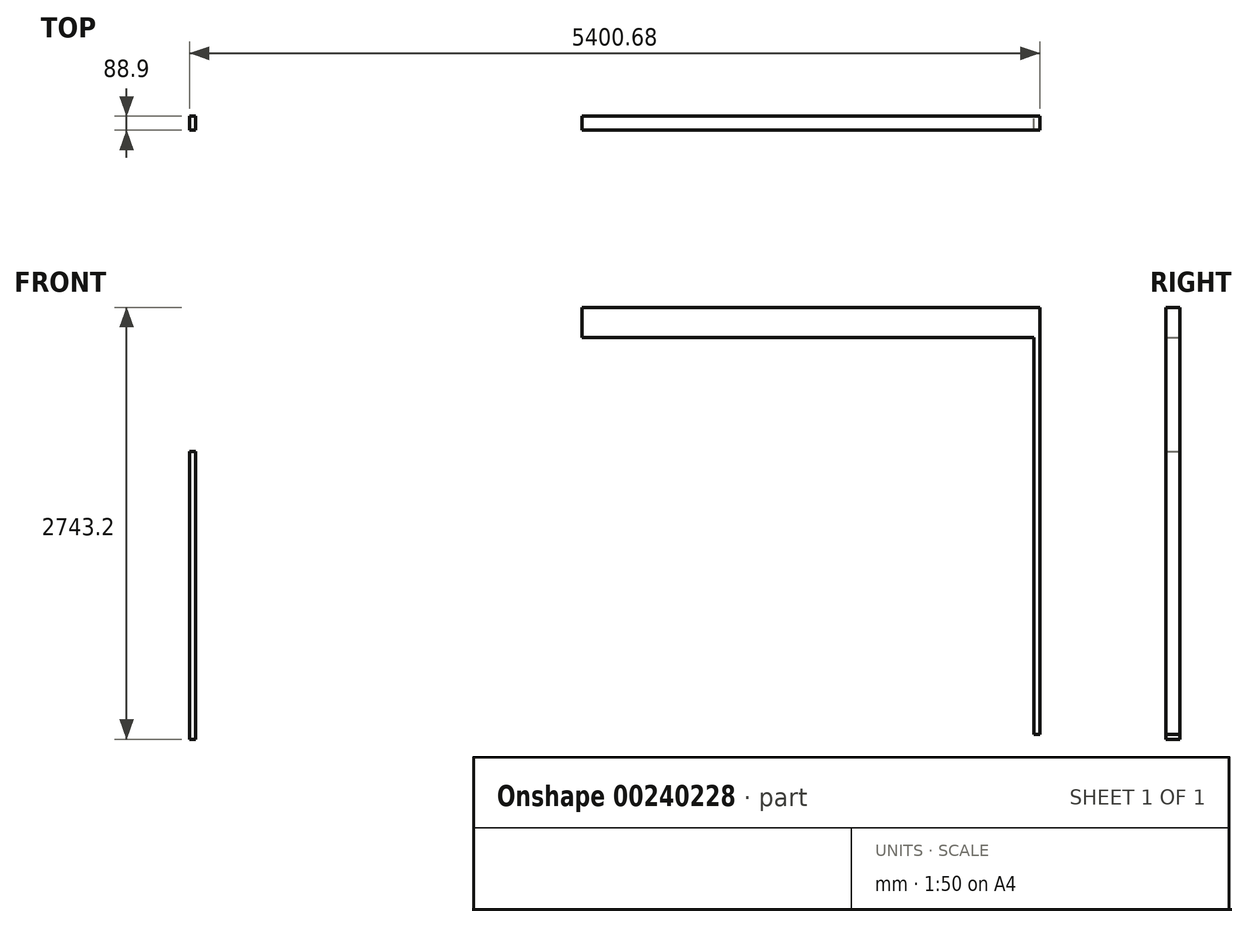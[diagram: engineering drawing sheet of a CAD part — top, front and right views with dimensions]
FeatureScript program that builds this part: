
annotation { "Feature Type Name" : "Feature", "Feature Type Description" : "" }
export const myFeature = defineFeature(function(context is Context, id is Id, definition is map)
    precondition{}
    {
        {
            var Q0;
            Q0=qCreatedBy(makeId("Front.planeOp"),FACE);
            var sketch = newSketch(context, id + "F0", { "sketchPlane" : qUnion([Q0])});
            skLineSegment(sketch, "E0", {"start": v(3075.3, -1602.17) * mm, "end": v(3075.3, 1229.93) * mm});
            skLineSegment(sketch, "E1", {"start": v(3075.3, 1541.08) * mm, "end": v(1348.1, 1541.08) * mm, "construction": true});
            skLineSegment(sketch, "E2", {"start": v(-3554.1, -1602.17) * mm, "end": v(-3554.1, 1541.08) * mm});
            skLineSegment(sketch, "E3", {"start": v(1348.1, 1541.08) * mm, "end": v(-3554.1, 1541.08) * mm});
            skLineSegment(sketch, "E4", {"start": v(1348.1, 1541.08) * mm, "end": v(3075.3, 1229.93) * mm});
            skLineSegment(sketch, "E5", {"start": v(3075.3, -1570.42) * mm, "end": v(-3554.1, -1570.42) * mm, "construction": true});
            skLineSegment(sketch, "E6", {"start": v(3075.3, 1141.03) * mm, "end": v(167, 1141.03) * mm});
            skLineSegment(sketch, "E7", {"start": v(3075.3, 950.53) * mm, "end": v(167, 950.53) * mm});
            skLineSegment(sketch, "E8", {"start": v(167, 950.53) * mm, "end": v(167, 1141.03) * mm});
            skLineSegment(sketch, "E9.bottom", {"start": v(205.1, 950.53) * mm, "end": v(167, 950.53) * mm});
            skLineSegment(sketch, "E9.top", {"start": v(205.1, -1602.17) * mm, "end": v(167, -1602.17) * mm});
            skLineSegment(sketch, "E9.left", {"start": v(205.1, 950.53) * mm, "end": v(205.1, -1602.17) * mm});
            skLineSegment(sketch, "E9.right", {"start": v(167, 950.53) * mm, "end": v(167, -1602.17) * mm});
            skLineSegment(sketch, "E10.bottom", {"start": v(167, 1541.08) * mm, "end": v(128.9, 1541.08) * mm});
            skLineSegment(sketch, "E10.top", {"start": v(167, -1602.17) * mm, "end": v(128.9, -1602.17) * mm});
            skLineSegment(sketch, "E10.left", {"start": v(167, 1541.08) * mm, "end": v(167, -1602.17) * mm});
            skLineSegment(sketch, "E10.right", {"start": v(128.9, 1541.08) * mm, "end": v(128.9, -1602.17) * mm});
            skLineSegment(sketch, "E11", {"start": v(-3150.88, -1602.17) * mm, "end": v(-3150.88, 226.63) * mm});
            skLineSegment(sketch, "E12", {"start": v(-2325.38, -1602.17) * mm, "end": v(-2325.38, 226.63) * mm});
            skLineSegment(sketch, "E13", {"start": v(-3150.88, 226.63) * mm, "end": v(-2325.38, 226.63) * mm});
            skLineSegment(sketch, "E14", {"start": v(-2325.38, -1602.17) * mm, "end": v(205.1, -1602.17) * mm});
            skLineSegment(sketch, "E15.bottom", {"start": v(979.8, 950.53) * mm, "end": v(1017.9, 950.53) * mm});
            skLineSegment(sketch, "E15.top", {"start": v(979.8, -1570.42) * mm, "end": v(1017.9, -1570.42) * mm});
            skLineSegment(sketch, "E15.left", {"start": v(979.8, 950.53) * mm, "end": v(979.8, -1570.42) * mm});
            skLineSegment(sketch, "E15.right", {"start": v(1017.9, 950.53) * mm, "end": v(1017.9, -1570.42) * mm});
            skLineSegment(sketch, "E16.bottom", {"start": v(573.4, 950.53) * mm, "end": v(611.5, 950.53) * mm});
            skLineSegment(sketch, "E16.top", {"start": v(573.4, -1570.42) * mm, "end": v(611.5, -1570.42) * mm});
            skLineSegment(sketch, "E16.left", {"start": v(573.4, 950.53) * mm, "end": v(573.4, -1570.42) * mm});
            skLineSegment(sketch, "E16.right", {"start": v(611.5, 950.53) * mm, "end": v(611.5, -1570.42) * mm});
            skLineSegment(sketch, "E17", {"start": v(-2325.38, 226.63) * mm, "end": v(-2287.28, 226.63) * mm});
            skLineSegment(sketch, "E18", {"start": v(-2287.28, 226.63) * mm, "end": v(-2287.28, -1602.17) * mm});
            skLineSegment(sketch, "E19", {"start": v(3037.2, 950.53) * mm, "end": v(3037.2, -1570.42) * mm});
            skLineSegment(sketch, "E20", {"start": v(3037.2, -1570.42) * mm, "end": v(3075.3, -1570.42) * mm});
            skSolve(sketch);
        }
        {
            var Q0;
            {var subQ0=sQuery(id+"F0.wireOp",EDGE,"E12");Q0=makeQuery(id+"F0.imprint","IMPRINT",FACE,{"disambiguationData":[TD([[makeQuery(id+"F0.imprint","IMPRINT",EDGE,{"derivedFrom":subQ0}),-1.0]])]});}
            var Q1;
            {var subQ4=sQuery(id+"F0.wireOp",EDGE,"E19");Q1=makeQuery(id+"F0.imprint","IMPRINT",FACE,{"disambiguationData":[TD([[makeQuery(id+"F0.imprint","IMPRINT",EDGE,{"derivedFrom":subQ4}),1.0]])]});}
            var Q2;
            Q2=makeQuery(id+"F0.imprint","IMPRINT",FACE,{"disambiguationData":[TD([[makeQuery(id+"F0.imprint","IMPRINT",EDGE,{"derivedFrom":sQuery(id+"F0.wireOp",EDGE,"E15.bottom")}),-1.0]])]});
            var Q3;
            Q3=makeQuery(id+"F0.imprint","IMPRINT",FACE,{"disambiguationData":[TD([[makeQuery(id+"F0.imprint","IMPRINT",EDGE,{"derivedFrom":sQuery(id+"F0.wireOp",EDGE,"E16.bottom")}),-1.0]])]});
            var Q4;
            {var subQ0=sQuery(id+"F0.wireOp",EDGE,"E9.bottom");Q4=makeQuery(id+"F0.imprint","IMPRINT",FACE,{"disambiguationData":[TD([[makeQuery(id+"F0.imprint","IMPRINT",EDGE,{"derivedFrom":subQ0}),1.0]])]});}
            var Q5;
            {var subQ5=sQuery(id+"F0.wireOp",EDGE,"E10.bottom");Q5=makeQuery(id+"F0.imprint","IMPRINT",FACE,{"disambiguationData":[TD([[makeQuery(id+"F0.imprint","IMPRINT",EDGE,{"derivedFrom":subQ5}),1.0]])]});}
            var Q6;
            {var subQ4=sQuery(id+"F0.wireOp",EDGE,"E6");Q6=makeQuery(id+"F0.imprint","IMPRINT",FACE,{"disambiguationData":[TD([[makeQuery(id+"F0.imprint","IMPRINT",EDGE,{"derivedFrom":subQ4}),1.0]])]});}
            extrude(context, id + "F1", {"entities" : qUnion([Q0, Q1, Q2, Q3, Q4, Q5, Q6]), "depth" : 88.9 * mm});
        }
    });
